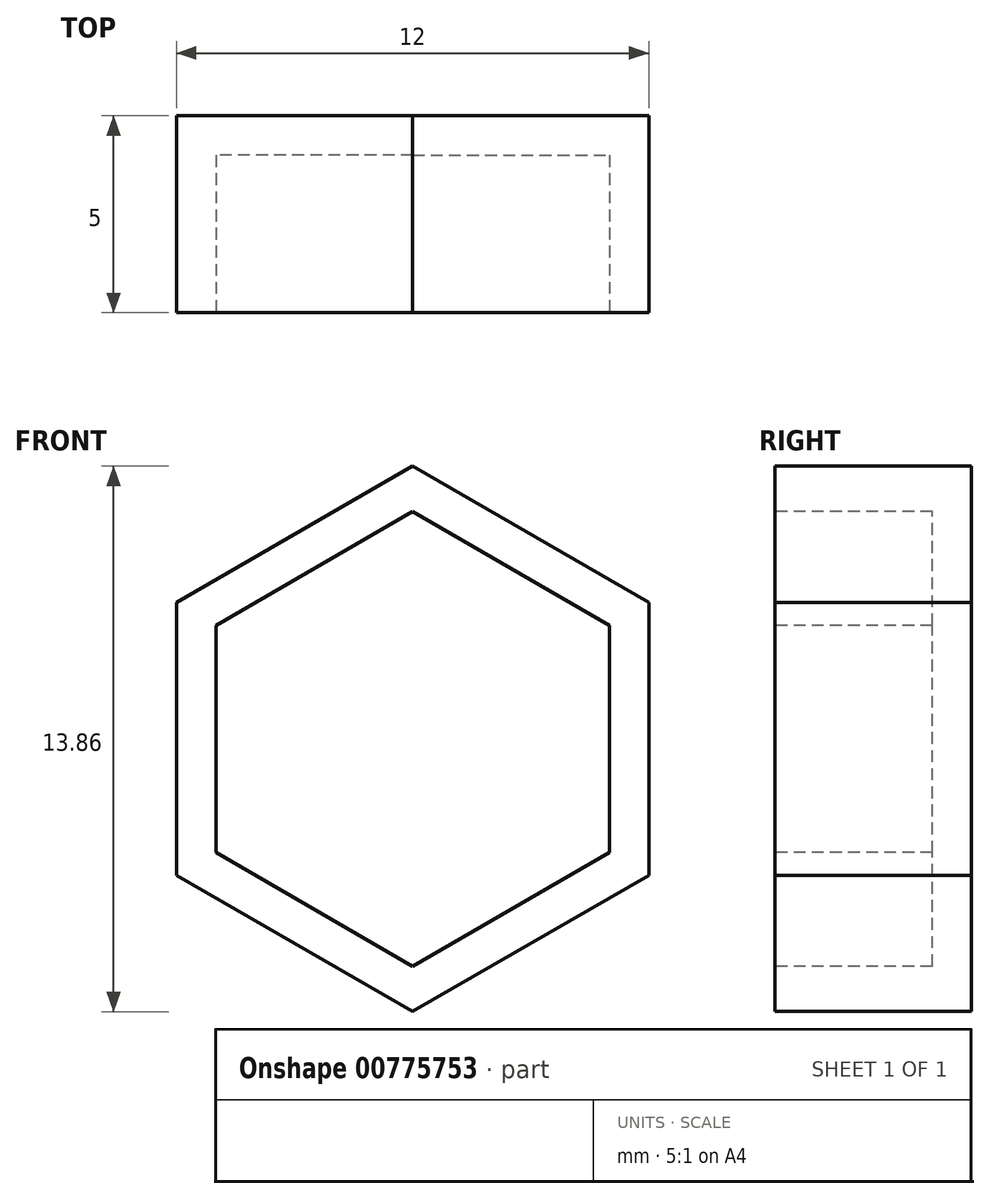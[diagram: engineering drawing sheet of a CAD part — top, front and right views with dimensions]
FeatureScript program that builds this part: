
annotation { "Feature Type Name" : "Feature", "Feature Type Description" : "" }
export const myFeature = defineFeature(function(context is Context, id is Id, definition is map)
    precondition{}
    {
        {
            var Q0;
            Q0=qCreatedBy(makeId("Front.planeOp"),FACE);
            var sketch = newSketch(context, id + "F0", { "sketchPlane" : qUnion([Q0])});
            skCircle(sketch, "E0.cCircle", {"center": v(0, 0) * mm, "radius": 5 * mm, "construction": true});
            skLineSegment(sketch, "E0.0", {"start": v(-5, -2.89) * mm, "end": v(-5, 2.89) * mm});
            skLineSegment(sketch, "E0.1", {"start": v(-5, 2.89) * mm, "end": v(0, 5.77) * mm});
            skLineSegment(sketch, "E0.2", {"start": v(0, 5.77) * mm, "end": v(5, 2.89) * mm});
            skLineSegment(sketch, "E0.3", {"start": v(5, 2.89) * mm, "end": v(5, -2.89) * mm});
            skLineSegment(sketch, "E0.4", {"start": v(5, -2.89) * mm, "end": v(0, -5.77) * mm});
            skLineSegment(sketch, "E0.5", {"start": v(0, -5.77) * mm, "end": v(-5, -2.89) * mm});
            skPoint(sketch, "E0.0.midPoint", {"position": v(-5, 0) * mm});
            skCircle(sketch, "E1.cCircle", {"center": v(0, 0) * mm, "radius": 6 * mm, "construction": true});
            skLineSegment(sketch, "E1.0", {"start": v(-6, 3.46) * mm, "end": v(0, 6.93) * mm});
            skLineSegment(sketch, "E1.1", {"start": v(0, 6.93) * mm, "end": v(6, 3.46) * mm});
            skLineSegment(sketch, "E1.2", {"start": v(6, 3.46) * mm, "end": v(6, -3.46) * mm});
            skLineSegment(sketch, "E1.3", {"start": v(6, -3.46) * mm, "end": v(0, -6.93) * mm});
            skLineSegment(sketch, "E1.4", {"start": v(0, -6.93) * mm, "end": v(-6, -3.46) * mm});
            skLineSegment(sketch, "E1.5", {"start": v(-6, -3.46) * mm, "end": v(-6, 3.46) * mm});
            skPoint(sketch, "E1.0.midPoint", {"position": v(-3, 5.2) * mm});
            skSolve(sketch);
        }
        {
            var Q0;
            Q0=makeQuery(id+"F0.imprint","IMPRINT",FACE,{"disambiguationData":[TD([[makeQuery(id+"F0.imprint","IMPRINT",EDGE,{"derivedFrom":sQuery(id+"F0.wireOp",EDGE,"E0.0")}),1.0]])]});
            extrude(context, id + "F1", {"entities" : qUnion([Q0]), "oppositeDirection" : true, "depth" : 5 * mm, "offsetDistance" : 25 * mm});
        }
        {
            var Q0;
            Q0=makeQuery(id+"F1.opExtrude","CAP_FACE",FACE,{"disambiguationData":[OSD([sQuery(id+"F0.wireOp",EDGE,"E0.0"),sQuery(id+"F0.wireOp",EDGE,"E0.1"),sQuery(id+"F0.wireOp",EDGE,"E0.2"),sQuery(id+"F0.wireOp",EDGE,"E0.3"),sQuery(id+"F0.wireOp",EDGE,"E0.4"),sQuery(id+"F0.wireOp",EDGE,"E0.5"),sQuery(id+"F0.wireOp",EDGE,"E1.0"),sQuery(id+"F0.wireOp",EDGE,"E1.1"),sQuery(id+"F0.wireOp",EDGE,"E1.2"),sQuery(id+"F0.wireOp",EDGE,"E1.3"),sQuery(id+"F0.wireOp",EDGE,"E1.4"),sQuery(id+"F0.wireOp",EDGE,"E1.5")])],"isStart":false});
            var sketch = newSketch(context, id + "F2", { "sketchPlane" : qUnion([Q0])});
            skCircle(sketch, "E2.cCircle", {"center": v(0, 0) * mm, "radius": 6 * mm, "construction": true});
            skLineSegment(sketch, "E2.0", {"start": v(0, 6.93) * mm, "end": v(6, 3.46) * mm});
            skLineSegment(sketch, "E2.1", {"start": v(6, 3.46) * mm, "end": v(6, -3.46) * mm});
            skLineSegment(sketch, "E2.2", {"start": v(6, -3.46) * mm, "end": v(0, -6.93) * mm});
            skLineSegment(sketch, "E2.3", {"start": v(0, -6.93) * mm, "end": v(-6, -3.46) * mm});
            skLineSegment(sketch, "E2.4", {"start": v(-6, -3.46) * mm, "end": v(-6, 3.46) * mm});
            skLineSegment(sketch, "E2.5", {"start": v(-6, 3.46) * mm, "end": v(0, 6.93) * mm});
            skPoint(sketch, "E2.0.midPoint", {"position": v(3, 5.2) * mm});
            skSolve(sketch);
        }
        {
            var Q0;
            Q0 = qSketchRegion(id + "F2", true);
            extrude(context, id + "F3", {"entities" : qUnion([Q0]), "operationType" : NewBodyOperationType.ADD, "oppositeDirection" : true, "depth" : 1 * mm, "offsetDistance" : 25 * mm});
        }
    });
